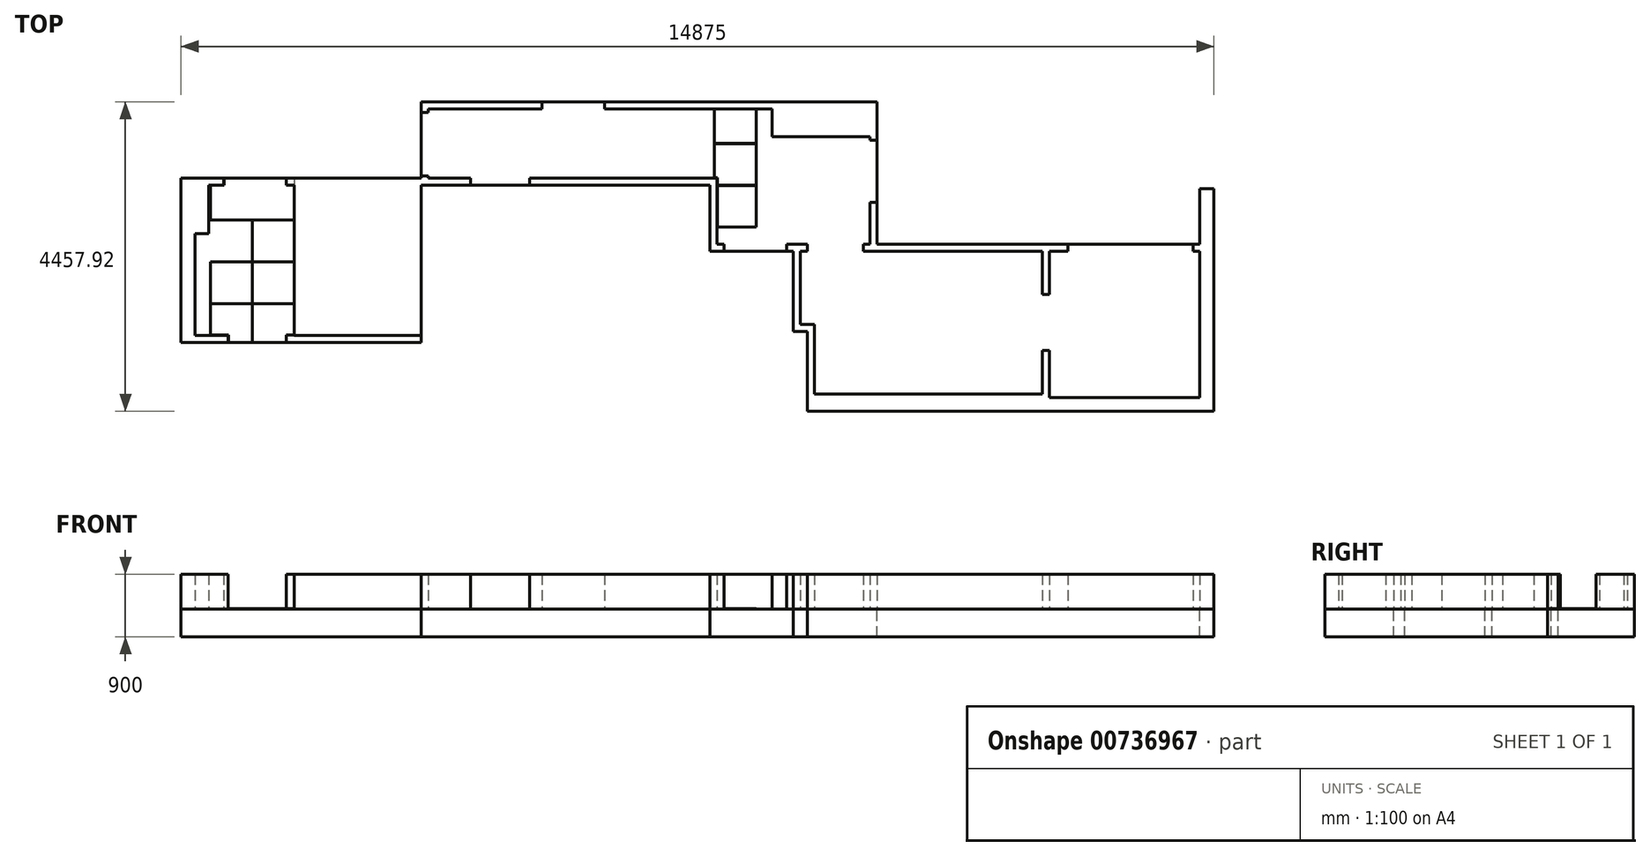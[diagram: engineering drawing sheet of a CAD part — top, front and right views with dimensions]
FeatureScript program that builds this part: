
annotation { "Feature Type Name" : "Feature", "Feature Type Description" : "" }
export const myFeature = defineFeature(function(context is Context, id is Id, definition is map)
    precondition{}
    {
        {
            var Q0;
            Q0=qCreatedBy(makeId("Top.planeOp"),FACE);
            var sketch = newSketch(context, id + "F0", { "sketchPlane" : qUnion([Q0])});
            skLineSegment(sketch, "E0.top", {"start": v(0, 2200) * mm, "end": v(-100, 2200) * mm});
            skLineSegment(sketch, "E0.left", {"start": v(0, 92.08) * mm, "end": v(0, 2200) * mm});
            skLineSegment(sketch, "E1", {"start": v(-1900, 2200) * mm, "end": v(-2168.75, 2200) * mm});
            skLineSegment(sketch, "E2", {"start": v(-4650, 2300) * mm, "end": v(0, 2300) * mm});
            skLineSegment(sketch, "E3.bottom", {"start": v(-1900, 2300) * mm, "end": v(-100, 2300) * mm});
            skLineSegment(sketch, "E3.left", {"start": v(-1900, 2300) * mm, "end": v(-1900, 2200) * mm});
            skLineSegment(sketch, "E3.right", {"start": v(-100, 2300) * mm, "end": v(-100, 2200) * mm});
            skLineSegment(sketch, "E4.bottom", {"start": v(-4650, 2200) * mm, "end": v(-4750, 2200) * mm});
            skLineSegment(sketch, "E4.top", {"start": v(-4650, 4350) * mm, "end": v(-4750, 4350) * mm});
            skLineSegment(sketch, "E4.left", {"start": v(-4650, 2300) * mm, "end": v(-4650, 4350) * mm});
            skLineSegment(sketch, "E4.right", {"start": v(-4750, 2300) * mm, "end": v(-4750, 2900) * mm});
            skLineSegment(sketch, "E5.bottom", {"start": v(-4750, 2900) * mm, "end": v(-4650, 2900) * mm});
            skLineSegment(sketch, "E5.top", {"start": v(-4750, 3800) * mm, "end": v(-4650, 3800) * mm});
            skLineSegment(sketch, "E5.right", {"start": v(-4650, 2900) * mm, "end": v(-4650, 3800) * mm});
            skLineSegment(sketch, "E6.bottom", {"start": v(-4650, 4350) * mm, "end": v(-8575, 4350) * mm});
            skLineSegment(sketch, "E6.top", {"start": v(-6160, 4250) * mm, "end": v(-8575, 4250) * mm});
            skLineSegment(sketch, "E6.left", {"start": v(-4650, 4350) * mm, "end": v(-4650, 4250) * mm});
            skLineSegment(sketch, "E6.right", {"start": v(-8575, 4350) * mm, "end": v(-8575, 4250) * mm});
            skLineSegment(sketch, "E7.trimOffspring", {"start": v(-4750, 3800) * mm, "end": v(-4750, 3850) * mm});
            skLineSegment(sketch, "E8.bottom", {"start": v(-8575, 4350) * mm, "end": v(-9475, 4350) * mm});
            skLineSegment(sketch, "E8.left", {"start": v(-8575, 4350) * mm, "end": v(-8575, 4245.37) * mm});
            skLineSegment(sketch, "E8.right", {"start": v(-9475, 4350) * mm, "end": v(-9475, 4250) * mm});
            skLineSegment(sketch, "E9.bottom", {"start": v(-9475, 4350) * mm, "end": v(-11115, 4350) * mm});
            skLineSegment(sketch, "E9.top", {"start": v(-9475, 4250) * mm, "end": v(-11115, 4250) * mm});
            skLineSegment(sketch, "E10.bottom", {"start": v(-11115, 4350) * mm, "end": v(-11215, 4350) * mm});
            skLineSegment(sketch, "E10.left", {"start": v(-11115, 4250) * mm, "end": v(-11115, 4195) * mm});
            skLineSegment(sketch, "E10.right", {"start": v(-11215, 4350) * mm, "end": v(-11215, 3250) * mm});
            skLineSegment(sketch, "E11.bottom", {"start": v(-11215, 4195) * mm, "end": v(-11115, 4195) * mm});
            skLineSegment(sketch, "E11.top", {"start": v(-11215, 3285) * mm, "end": v(-11115, 3285) * mm});
            skLineSegment(sketch, "E11.left", {"start": v(-11215, 4195) * mm, "end": v(-11215, 3285) * mm});
            skLineSegment(sketch, "E12.trimOffspring", {"start": v(-11115, 3285) * mm, "end": v(-11115, 3250) * mm});
            skLineSegment(sketch, "E13.bottom", {"start": v(-11115, 3250) * mm, "end": v(-10505.7, 3250) * mm});
            skLineSegment(sketch, "E13.top", {"start": v(-11215, 3150) * mm, "end": v(-7055.7, 3150) * mm});
            skLineSegment(sketch, "E13.right", {"start": v(-6955.7, 3250) * mm, "end": v(-6955.7, 3150) * mm});
            skLineSegment(sketch, "E14.bottom", {"start": v(-13045, 3150) * mm, "end": v(-13160, 3150) * mm});
            skLineSegment(sketch, "E14.top", {"start": v(-11215, 885) * mm, "end": v(-14475, 885) * mm});
            skLineSegment(sketch, "E14.left", {"start": v(-11215, 3150) * mm, "end": v(-11215, 885) * mm});
            skLineSegment(sketch, "E14.right", {"start": v(-14475, 2450) * mm, "end": v(-14475, 985) * mm});
            skLineSegment(sketch, "E15.top", {"start": v(-11215, 985) * mm, "end": v(-13155, 985) * mm});
            skLineSegment(sketch, "E15.left", {"start": v(-11215, 3285) * mm, "end": v(-11215, 985) * mm});
            skLineSegment(sketch, "E15.right", {"start": v(-14675, 3250) * mm, "end": v(-14675, 985) * mm});
            skLineSegment(sketch, "E16.top", {"start": v(-14475, 2450) * mm, "end": v(-14275, 2450) * mm});
            skLineSegment(sketch, "E16.right", {"start": v(-14275, 3150) * mm, "end": v(-14275, 2450) * mm});
            skLineSegment(sketch, "E17.top", {"start": v(-13045, 985) * mm, "end": v(-12945, 985) * mm});
            skLineSegment(sketch, "E17.left", {"start": v(-13045, 3150) * mm, "end": v(-13045, 985) * mm});
            skLineSegment(sketch, "E17.right", {"start": v(-12945, 3150) * mm, "end": v(-12945, 985) * mm});
            skLineSegment(sketch, "E18", {"start": v(-11215, 3250) * mm, "end": v(-14675, 3250) * mm});
            skLineSegment(sketch, "E19.top", {"start": v(-14675, 885) * mm, "end": v(-14475, 885) * mm});
            skLineSegment(sketch, "E19.left", {"start": v(-14675, 985) * mm, "end": v(-14675, 885) * mm});
            skLineSegment(sketch, "E20.top", {"start": v(-13995, 885) * mm, "end": v(-13155, 885) * mm});
            skLineSegment(sketch, "E20.left", {"start": v(-13995, 985) * mm, "end": v(-13995, 885) * mm});
            skLineSegment(sketch, "E20.right", {"start": v(-13155, 985) * mm, "end": v(-13155, 885) * mm});
            skLineSegment(sketch, "E21.bottom", {"start": v(-14060, 3250) * mm, "end": v(-13160, 3250) * mm});
            skLineSegment(sketch, "E21.left", {"start": v(-14060, 3250) * mm, "end": v(-14060, 3150) * mm});
            skLineSegment(sketch, "E21.right", {"start": v(-13160, 3250) * mm, "end": v(-13160, 3150) * mm});
            skLineSegment(sketch, "E22.trimOffspring", {"start": v(-14060, 3150) * mm, "end": v(-14275, 3150) * mm});
            skLineSegment(sketch, "E23.trimOffspring", {"start": v(-13995, 985) * mm, "end": v(-14475, 985) * mm});
            skLineSegment(sketch, "E24.top", {"start": v(-6955.7, 2300) * mm, "end": v(-6855.7, 2300) * mm});
            skLineSegment(sketch, "E24.left", {"start": v(-6955.7, 3250) * mm, "end": v(-6955.7, 2300) * mm});
            skLineSegment(sketch, "E24.right", {"start": v(-4650, 3250) * mm, "end": v(-4650, 2300) * mm});
            skLineSegment(sketch, "E25.bottom", {"start": v(-7055.7, 3250) * mm, "end": v(-6955.7, 3250) * mm});
            skLineSegment(sketch, "E25.top", {"start": v(-7055.7, 2200) * mm, "end": v(-5855.7, 2200) * mm});
            skLineSegment(sketch, "E25.left", {"start": v(-7055.7, 3150) * mm, "end": v(-7055.7, 2200) * mm});
            skLineSegment(sketch, "E26.top", {"start": v(-6855.7, 2200) * mm, "end": v(-5955.7, 2200) * mm});
            skLineSegment(sketch, "E26.left", {"start": v(-6855.7, 2300) * mm, "end": v(-6855.7, 2200) * mm});
            skLineSegment(sketch, "E26.right", {"start": v(-5955.7, 2300) * mm, "end": v(-5955.7, 2200) * mm});
            skLineSegment(sketch, "E27.trimOffspring", {"start": v(-5955.7, 2300) * mm, "end": v(-5655.7, 2300) * mm});
            skLineSegment(sketch, "E28.bottom", {"start": v(-12945, 3150) * mm, "end": v(-11215, 3150) * mm});
            skLineSegment(sketch, "E28.top", {"start": v(-12945, 3250) * mm, "end": v(-11215, 3250) * mm});
            skLineSegment(sketch, "E29.top", {"start": v(-6160, 3850) * mm, "end": v(-4750, 3850) * mm});
            skLineSegment(sketch, "E29.left", {"start": v(-6160, 4250) * mm, "end": v(-6160, 3850) * mm});
            skPoint(sketch, "E30.orphan", {"position": v(-4750, 4250) * mm});
            skLineSegment(sketch, "E31.left", {"start": v(-5655.7, 2300) * mm, "end": v(-5655.7, 2200) * mm});
            skLineSegment(sketch, "E31.right", {"start": v(-4850, 2300) * mm, "end": v(-4850, 2200) * mm});
            skLineSegment(sketch, "E32.left", {"start": v(-5855.7, 2200) * mm, "end": v(-5855.7, 1042.08) * mm});
            skLineSegment(sketch, "E32.right", {"start": v(-5755.7, 2200) * mm, "end": v(-5755.7, 1142.08) * mm});
            skLineSegment(sketch, "E33.bottom", {"start": v(0, 3100) * mm, "end": v(200, 3100) * mm});
            skLineSegment(sketch, "E33.left", {"start": v(0, 3100) * mm, "end": v(0, 2300) * mm});
            skLineSegment(sketch, "E33.right", {"start": v(200, 3100) * mm, "end": v(200, 0) * mm});
            skLineSegment(sketch, "E34.trimOffspring", {"start": v(0, 2200) * mm, "end": v(0, 92.08) * mm});
            skLineSegment(sketch, "E35.left", {"start": v(0, 0) * mm, "end": v(0, 0) * mm});
            skLineSegment(sketch, "E36.trimOffspring", {"start": v(-4850, 2300) * mm, "end": v(-4750, 2300) * mm});
            skLineSegment(sketch, "E37.trimOffspring", {"start": v(-4850, 2200) * mm, "end": v(-4650, 2200) * mm});
            skLineSegment(sketch, "E38.top", {"start": v(-5655.7, -107.92) * mm, "end": v(200, -107.92) * mm});
            skLineSegment(sketch, "E38.right", {"start": v(200, 142.08) * mm, "end": v(200, -107.92) * mm});
            skLineSegment(sketch, "E39.bottom", {"start": v(-5855.7, 1042.08) * mm, "end": v(-5655.7, 1042.08) * mm});
            skLineSegment(sketch, "E39.right", {"start": v(-5655.7, 1042.08) * mm, "end": v(-5655.7, -107.92) * mm});
            skLineSegment(sketch, "E40.bottom", {"start": v(-5755.7, 1142.08) * mm, "end": v(-5555.7, 1142.08) * mm});
            skLineSegment(sketch, "E40.right", {"start": v(-5555.7, 1142.08) * mm, "end": v(-5555.7, 142.08) * mm});
            skLineSegment(sketch, "E41.trimOffspring", {"start": v(-5555.7, 142.08) * mm, "end": v(-2268.75, 142.08) * mm});
            skLineSegment(sketch, "E42.left", {"start": v(-2168.75, 2200) * mm, "end": v(-2168.75, 1575) * mm});
            skLineSegment(sketch, "E42.right", {"start": v(-2268.75, 2200) * mm, "end": v(-2268.75, 1575) * mm});
            skLineSegment(sketch, "E43.trimOffspring", {"start": v(-2268.75, 2200) * mm, "end": v(-4650, 2200) * mm});
            skLineSegment(sketch, "E44.trimOffspring", {"start": v(0, 142.08) * mm, "end": v(200, 142.08) * mm});
            skLineSegment(sketch, "E45.trimOffspring", {"start": v(-2268.75, 142.08) * mm, "end": v(-5555.7, 142.08) * mm});
            skLineSegment(sketch, "E46", {"start": v(-4482.54, 1242.08) * mm, "end": v(-1007.3, 1242.08) * mm, "construction": true});
            skLineSegment(sketch, "E47.bottom", {"start": v(-2268.75, 1575) * mm, "end": v(-2168.75, 1575) * mm});
            skLineSegment(sketch, "E47.top", {"start": v(-2268.75, 767.08) * mm, "end": v(-2168.75, 767.08) * mm});
            skLineSegment(sketch, "E48.bottom", {"start": v(-2268.75, 1575) * mm, "end": v(-2268.75, 1575) * mm});
            skLineSegment(sketch, "E48.top", {"start": v(-2268.75, 767.08) * mm, "end": v(-2268.75, 767.08) * mm});
            skLineSegment(sketch, "E49.top", {"start": v(-2168.75, 92.08) * mm, "end": v(0, 92.08) * mm});
            skLineSegment(sketch, "E49.left", {"start": v(-2168.75, 142.08) * mm, "end": v(-2168.75, 92.08) * mm});
            skLineSegment(sketch, "E49.right", {"start": v(0, 142.08) * mm, "end": v(0, 92.08) * mm});
            skLineSegment(sketch, "E50.trimOffspring", {"start": v(-5755.7, 2200) * mm, "end": v(-5655.7, 2200) * mm});
            skLineSegment(sketch, "E51.trimOffspring", {"start": v(-2168.75, 767.08) * mm, "end": v(-2168.75, 142.08) * mm});
            skLineSegment(sketch, "E52.trimOffspring", {"start": v(-2268.75, 767.08) * mm, "end": v(-2268.75, 142.08) * mm});
            skLineSegment(sketch, "E53.top", {"start": v(-10505.7, 3150) * mm, "end": v(-9655.7, 3150) * mm});
            skLineSegment(sketch, "E53.left", {"start": v(-10505.7, 3250) * mm, "end": v(-10505.7, 3150) * mm});
            skLineSegment(sketch, "E53.right", {"start": v(-9655.7, 3250) * mm, "end": v(-9655.7, 3150) * mm});
            skLineSegment(sketch, "E54.trimOffspring", {"start": v(-9655.7, 3250) * mm, "end": v(-6955.7, 3250) * mm});
            skSolve(sketch);
        }
        {
            var Q0;
            Q0 = qSketchRegion(id + "F0", true);
            extrude(context, id + "F1", {"entities" : qUnion([Q0]), "oppositeDirection" : true, "depth" : 400 * mm, "offsetDistance" : 25 * mm});
        }
        {
            var Q0;
            Q0=makeQuery(id+"F0.imprint","IMPRINT",FACE,{"disambiguationData":[TD([[makeQuery(id+"F0.imprint","IMPRINT",EDGE,{"derivedFrom":sQuery(id+"F0.wireOp",EDGE,"E9.bottom")}),1.0]])]});
            var Q1;
            Q1=makeQuery(id+"F0.imprint","IMPRINT",FACE,{"disambiguationData":[TD([[makeQuery(id+"F0.imprint","IMPRINT",EDGE,{"derivedFrom":sQuery(id+"F0.wireOp",EDGE,"E4.left")}),1.0]])]});
            var Q2;
            {var subQ4=sQuery(id+"F0.wireOp",EDGE,"E11.top");Q2=makeQuery(id+"F0.imprint","IMPRINT",FACE,{"disambiguationData":[TD([[makeQuery(id+"F0.imprint","IMPRINT",EDGE,{"derivedFrom":subQ4}),-1.0]])]});}
            var Q3;
            Q3=makeQuery(id+"F0.imprint","IMPRINT",FACE,{"disambiguationData":[TD([[makeQuery(id+"F0.imprint","IMPRINT",EDGE,{"derivedFrom":sQuery(id+"F0.wireOp",EDGE,"E14.bottom")}),-1.0]])]});
            var Q4;
            Q4=makeQuery(id+"F0.imprint","IMPRINT",FACE,{"disambiguationData":[TD([[makeQuery(id+"F0.imprint","IMPRINT",EDGE,{"derivedFrom":sQuery(id+"F0.wireOp",EDGE,"E14.right")}),-1.0]])]});
            var Q5;
            {var subQ1=sQuery(id+"F0.wireOp",EDGE,"E14.left");Q5=makeQuery(id+"F0.imprint","IMPRINT",FACE,{"disambiguationData":[TD([[makeQuery(id+"F0.imprint","IMPRINT",EDGE,{"derivedFrom":subQ1}),-1.0]])]});}
            var Q6;
            {var subQ7=sQuery(id+"F0.wireOp",EDGE,"E26.right");Q6=makeQuery(id+"F0.imprint","IMPRINT",FACE,{"disambiguationData":[TD([[makeQuery(id+"F0.imprint","IMPRINT",EDGE,{"derivedFrom":subQ7}),1.0]])]});}
            var Q7;
            Q7=makeQuery(id+"F0.imprint","IMPRINT",FACE,{"disambiguationData":[TD([[makeQuery(id+"F0.imprint","IMPRINT",EDGE,{"derivedFrom":sQuery(id+"F0.wireOp",EDGE,"E1")}),-1.0]])]});
            var Q8;
            {var subQ0=sQuery(id+"F0.wireOp",EDGE,"E0.top");Q8=makeQuery(id+"F0.imprint","IMPRINT",FACE,{"disambiguationData":[TD([[makeQuery(id+"F0.imprint","IMPRINT",EDGE,{"derivedFrom":subQ0}),-1.0]])]});}
            var Q9;
            {var subQ1=sQuery(id+"F0.wireOp",EDGE,"E24.top");Q9=makeQuery(id+"F0.imprint","IMPRINT",FACE,{"disambiguationData":[TD([[makeQuery(id+"F0.imprint","IMPRINT",EDGE,{"derivedFrom":subQ1}),-1.0]])]});}
            extrude(context, id + "F2", {"entities" : qUnion([Q0, Q1, Q2, Q3, Q4, Q5, Q6, Q7, Q8, Q9]), "depth" : 500 * mm, "offsetDistance" : 25 * mm});
        }
        {
            var Q0;
            Q0=makeQuery(id+"F1.opExtrude","CAP_FACE",FACE,{"disambiguationData":[OSD([sQuery(id+"F0.wireOp",EDGE,"E2"),sQuery(id+"F0.wireOp",EDGE,"E3.bottom"),sQuery(id+"F0.wireOp",EDGE,"E4.left"),sQuery(id+"F0.wireOp",EDGE,"E5.right"),sQuery(id+"F0.wireOp",EDGE,"E6.bottom"),sQuery(id+"F0.wireOp",EDGE,"E6.left"),sQuery(id+"F0.wireOp",EDGE,"E8.bottom"),sQuery(id+"F0.wireOp",EDGE,"E9.bottom"),sQuery(id+"F0.wireOp",EDGE,"E10.bottom"),sQuery(id+"F0.wireOp",EDGE,"E10.right"),sQuery(id+"F0.wireOp",EDGE,"E11.left"),sQuery(id+"F0.wireOp",EDGE,"E13.top"),sQuery(id+"F0.wireOp",EDGE,"E14.top"),sQuery(id+"F0.wireOp",EDGE,"E14.left"),sQuery(id+"F0.wireOp",EDGE,"E15.left"),sQuery(id+"F0.wireOp",EDGE,"E15.right"),sQuery(id+"F0.wireOp",EDGE,"E18"),sQuery(id+"F0.wireOp",EDGE,"E19.top"),sQuery(id+"F0.wireOp",EDGE,"E19.left"),sQuery(id+"F0.wireOp",EDGE,"E20.top"),sQuery(id+"F0.wireOp",EDGE,"E21.bottom"),sQuery(id+"F0.wireOp",EDGE,"E25.top"),sQuery(id+"F0.wireOp",EDGE,"E25.left"),sQuery(id+"F0.wireOp",EDGE,"E24.right"),sQuery(id+"F0.wireOp",EDGE,"E26.top"),sQuery(id+"F0.wireOp",EDGE,"E28.top"),sQuery(id+"F0.wireOp",EDGE,"E33.bottom"),sQuery(id+"F0.wireOp",EDGE,"E33.left"),sQuery(id+"F0.wireOp",EDGE,"E33.right"),sQuery(id+"F0.wireOp",EDGE,"E32.left"),sQuery(id+"F0.wireOp",EDGE,"E38.top"),sQuery(id+"F0.wireOp",EDGE,"E38.right"),sQuery(id+"F0.wireOp",EDGE,"E39.bottom"),sQuery(id+"F0.wireOp",EDGE,"E39.right")])],"isStart":true});
            var sketch = newSketch(context, id + "F3", { "sketchPlane" : qUnion([Q0])});
            skLineSegment(sketch, "E55", {"start": v(-11232.86, 3750) * mm, "end": v(-6657.9, 3750) * mm, "construction": true});
            skLineSegment(sketch, "E56", {"start": v(-6601.23, 1100) * mm, "end": v(377.65, 1100) * mm, "construction": true});
            skLineSegment(sketch, "E57", {"start": v(-13646.5, 3585.93) * mm, "end": v(-13646.5, 518.44) * mm, "construction": true});
            skLineSegment(sketch, "E58.bottom", {"start": v(-13646.5, 2647) * mm, "end": v(-13046.5, 2647) * mm});
            skLineSegment(sketch, "E58.top", {"start": v(-13646.5, 2047) * mm, "end": v(-13046.5, 2047) * mm});
            skLineSegment(sketch, "E58.left", {"start": v(-13646.5, 2647) * mm, "end": v(-13646.5, 2047) * mm});
            skLineSegment(sketch, "E58.right", {"start": v(-13046.5, 2647) * mm, "end": v(-13046.5, 2047) * mm});
            skLineSegment(sketch, "E59.bottom", {"start": v(-13649.5, 2647) * mm, "end": v(-14249.5, 2647) * mm});
            skLineSegment(sketch, "E59.top", {"start": v(-13649.5, 2047) * mm, "end": v(-14249.5, 2047) * mm});
            skLineSegment(sketch, "E59.right", {"start": v(-14249.5, 2647) * mm, "end": v(-14249.5, 2047) * mm});
            skLineSegment(sketch, "E60.bottom", {"start": v(-14249.5, 2647) * mm, "end": v(-13649.5, 2647) * mm});
            skLineSegment(sketch, "E60.top", {"start": v(-14249.5, 2047) * mm, "end": v(-13649.5, 2047) * mm});
            skLineSegment(sketch, "E60.right", {"start": v(-13649.5, 2647) * mm, "end": v(-13649.5, 2047) * mm});
            skLineSegment(sketch, "E61.bottom", {"start": v(-13646.5, 3250) * mm, "end": v(-13042.88, 3250) * mm});
            skLineSegment(sketch, "E61.top", {"start": v(-13646.5, 2650) * mm, "end": v(-13042.88, 2650) * mm});
            skLineSegment(sketch, "E61.left", {"start": v(-13646.5, 3250) * mm, "end": v(-13646.5, 2650) * mm});
            skLineSegment(sketch, "E61.right", {"start": v(-13042.88, 3250) * mm, "end": v(-13042.88, 2650) * mm});
            skLineSegment(sketch, "E62.bottom", {"start": v(-14249.5, 2650) * mm, "end": v(-13646.5, 2650) * mm});
            skLineSegment(sketch, "E62.top", {"start": v(-14057, 3250) * mm, "end": v(-13646.5, 3250) * mm});
            skLineSegment(sketch, "E62.left", {"start": v(-14249.5, 2650) * mm, "end": v(-14249.5, 3147) * mm});
            skLineSegment(sketch, "E62.right", {"start": v(-13646.5, 2650) * mm, "end": v(-13646.5, 3250) * mm});
            skLineSegment(sketch, "E63", {"start": v(-14249.5, 3147) * mm, "end": v(-14057, 3147) * mm});
            skLineSegment(sketch, "E64", {"start": v(-14057, 3147) * mm, "end": v(-14057, 3250) * mm});
            skLineSegment(sketch, "E65", {"start": v(-13163, 3250) * mm, "end": v(-13163, 3147) * mm});
            skLineSegment(sketch, "E66", {"start": v(-13163, 3147) * mm, "end": v(-13042.88, 3147) * mm});
            skLineSegment(sketch, "E67.bottom", {"start": v(-14249.5, 2044) * mm, "end": v(-13649.5, 2044) * mm});
            skLineSegment(sketch, "E67.top", {"start": v(-14249.5, 1444) * mm, "end": v(-13649.5, 1444) * mm});
            skLineSegment(sketch, "E67.left", {"start": v(-14249.5, 2044) * mm, "end": v(-14249.5, 1444) * mm});
            skLineSegment(sketch, "E67.right", {"start": v(-13649.5, 2044) * mm, "end": v(-13649.5, 1444) * mm});
            skLineSegment(sketch, "E68.bottom", {"start": v(-13646.5, 2044) * mm, "end": v(-13046.5, 2044) * mm});
            skLineSegment(sketch, "E68.top", {"start": v(-13646.5, 1444) * mm, "end": v(-13046.5, 1444) * mm});
            skLineSegment(sketch, "E68.left", {"start": v(-13646.5, 2044) * mm, "end": v(-13646.5, 1444) * mm});
            skLineSegment(sketch, "E68.right", {"start": v(-13046.5, 2044) * mm, "end": v(-13046.5, 1444) * mm});
            skLineSegment(sketch, "E69.bottom", {"start": v(-14249.5, 1441) * mm, "end": v(-13649.5, 1441) * mm});
            skLineSegment(sketch, "E69.left", {"start": v(-14249.5, 1441) * mm, "end": v(-14249.5, 988) * mm});
            skLineSegment(sketch, "E69.right", {"start": v(-13649.5, 1441) * mm, "end": v(-13649.5, 885) * mm});
            skLineSegment(sketch, "E70.bottom", {"start": v(-13646.5, 1441) * mm, "end": v(-13046.5, 1441) * mm});
            skLineSegment(sketch, "E70.left", {"start": v(-13646.5, 1441) * mm, "end": v(-13646.5, 841) * mm});
            skLineSegment(sketch, "E70.right", {"start": v(-13046.5, 1441) * mm, "end": v(-13046.5, 988) * mm});
            skLineSegment(sketch, "E71", {"start": v(-14249.5, 988) * mm, "end": v(-13992, 988) * mm});
            skLineSegment(sketch, "E72", {"start": v(-13992, 988) * mm, "end": v(-13992, 885) * mm});
            skLineSegment(sketch, "E73", {"start": v(-13158, 885) * mm, "end": v(-13158, 988) * mm});
            skLineSegment(sketch, "E74", {"start": v(-13158, 988) * mm, "end": v(-13046.5, 988) * mm});
            skLineSegment(sketch, "E75", {"start": v(-13992, 885) * mm, "end": v(-13649.5, 885) * mm});
            skLineSegment(sketch, "E76", {"start": v(-13646.5, 885) * mm, "end": v(-13158, 885) * mm});
            skLineSegment(sketch, "E77.bottom", {"start": v(-6950.7, 3148.5) * mm, "end": v(-6394, 3148.5) * mm});
            skLineSegment(sketch, "E77.top", {"start": v(-6954.2, 3748.5) * mm, "end": v(-6394, 3748.5) * mm});
            skLineSegment(sketch, "E78.bottom", {"start": v(-6950.7, 3145.5) * mm, "end": v(-6394, 3145.5) * mm});
            skLineSegment(sketch, "E78.top", {"start": v(-6950.7, 2545.5) * mm, "end": v(-6394, 2545.5) * mm});
            skLineSegment(sketch, "E78.left", {"start": v(-6950.7, 3145.5) * mm, "end": v(-6950.7, 2545.5) * mm});
            skLineSegment(sketch, "E79.bottom", {"start": v(-6954.2, 3751.5) * mm, "end": v(-6394, 3751.5) * mm});
            skLineSegment(sketch, "E79.top", {"start": v(-6954.2, 4247) * mm, "end": v(-6394, 4247) * mm});
            skLineSegment(sketch, "E80.left", {"start": v(-11215, 3751.5) * mm, "end": v(-11215, 4190) * mm});
            skLineSegment(sketch, "E80.right", {"start": v(-10615, 3751.5) * mm, "end": v(-10615, 4244.92) * mm});
            skLineSegment(sketch, "E81.bottom", {"start": v(-11215, 4190) * mm, "end": v(-11110, 4190) * mm});
            skLineSegment(sketch, "E81.right", {"start": v(-11110, 4190) * mm, "end": v(-11110, 4244.92) * mm});
            skLineSegment(sketch, "E82", {"start": v(-11215, 3751.5) * mm, "end": v(-10615, 3751.5) * mm});
            skPoint(sketch, "E83.orphan", {"position": v(-11215, 3800) * mm});
            skLineSegment(sketch, "E84.MirrorCS", {"start": v(-11215, 3748.5) * mm, "end": v(-10615, 3748.5) * mm});
            skLineSegment(sketch, "E85.MirrorCS", {"start": v(-10615, 3748.5) * mm, "end": v(-10615, 3255) * mm});
            skLineSegment(sketch, "E86.MirrorCS", {"start": v(-11110, 3290.7) * mm, "end": v(-11110, 3255) * mm});
            skLineSegment(sketch, "E87.MirrorCS", {"start": v(-11215, 3748.5) * mm, "end": v(-11215, 3310) * mm});
            skLineSegment(sketch, "E88", {"start": v(-11215, 3290.7) * mm, "end": v(-11110, 3290.7) * mm});
            skPoint(sketch, "E89.orphan", {"position": v(-11110, 3310) * mm});
            skLineSegment(sketch, "E90", {"start": v(-11215, 3290.7) * mm, "end": v(-11215, 3310) * mm});
            skLineSegment(sketch, "E91", {"start": v(-11110, 3255) * mm, "end": v(-10615, 3255) * mm});
            skPoint(sketch, "E92.MirrorCS.start.orphan", {"position": v(-11110, 3248) * mm});
            skPoint(sketch, "E93.orphan", {"position": v(-10615, 3248) * mm});
            skLineSegment(sketch, "E94", {"start": v(-11110, 4244.92) * mm, "end": v(-10615, 4244.92) * mm});
            skPoint(sketch, "E95.orphan", {"position": v(-10615, 4252) * mm});
            skPoint(sketch, "E96.orphan", {"position": v(-11110, 4252) * mm});
            skLineSegment(sketch, "E97.bottom", {"start": v(-10612, 4244.92) * mm, "end": v(-10012, 4244.92) * mm});
            skLineSegment(sketch, "E97.top", {"start": v(-10612, 3751.5) * mm, "end": v(-10012, 3751.5) * mm});
            skLineSegment(sketch, "E97.left", {"start": v(-10612, 4244.92) * mm, "end": v(-10612, 3751.5) * mm});
            skLineSegment(sketch, "E97.right", {"start": v(-10012, 4244.92) * mm, "end": v(-10012, 3751.5) * mm});
            skLineSegment(sketch, "E98.bottom", {"start": v(-10612, 3748.5) * mm, "end": v(-10012, 3748.5) * mm});
            skLineSegment(sketch, "E98.top", {"start": v(-10503.7, 3148.5) * mm, "end": v(-10012, 3148.5) * mm});
            skLineSegment(sketch, "E98.left", {"start": v(-10612, 3748.5) * mm, "end": v(-10612, 3255) * mm});
            skLineSegment(sketch, "E98.right", {"start": v(-10012, 3748.5) * mm, "end": v(-10012, 3148.5) * mm});
            skLineSegment(sketch, "E99.bottom", {"start": v(-10612, 3255) * mm, "end": v(-10503.7, 3255) * mm});
            skLineSegment(sketch, "E99.top", {"start": v(-10615, 3148.5) * mm, "end": v(-10612, 3148.5) * mm});
            skLineSegment(sketch, "E99.right", {"start": v(-10503.7, 3255) * mm, "end": v(-10503.7, 3148.5) * mm});
            skLineSegment(sketch, "E100.bottom", {"start": v(-10009, 3751.5) * mm, "end": v(-9409, 3751.5) * mm});
            skLineSegment(sketch, "E100.top", {"start": v(-10009, 4244.92) * mm, "end": v(-9468.1, 4244.92) * mm});
            skLineSegment(sketch, "E100.left", {"start": v(-10009, 3751.5) * mm, "end": v(-10009, 4244.92) * mm});
            skLineSegment(sketch, "E100.right", {"start": v(-9409, 3751.5) * mm, "end": v(-9409, 4244.92) * mm});
            skLineSegment(sketch, "E101.top", {"start": v(-9468.1, 4350) * mm, "end": v(-9409, 4350) * mm});
            skLineSegment(sketch, "E101.left", {"start": v(-9468.1, 4244.92) * mm, "end": v(-9468.1, 4350) * mm});
            skLineSegment(sketch, "E101.right", {"start": v(-9409, 4244.92) * mm, "end": v(-9409, 4350) * mm});
            skPoint(sketch, "E102.0", {"position": v(-9475, 4300) * mm});
            skLineSegment(sketch, "E103.0", {"start": v(-9475, 4350) * mm, "end": v(-9475, 4250) * mm});
            skLineSegment(sketch, "E104.bottom", {"start": v(-10009, 3748.5) * mm, "end": v(-9409, 3748.5) * mm});
            skLineSegment(sketch, "E104.top", {"start": v(-10009, 3150) * mm, "end": v(-9660.7, 3150) * mm});
            skLineSegment(sketch, "E104.left", {"start": v(-10009, 3748.5) * mm, "end": v(-10009, 3150) * mm});
            skLineSegment(sketch, "E104.right", {"start": v(-9409, 3748.5) * mm, "end": v(-9409, 3255) * mm});
            skLineSegment(sketch, "E105.top", {"start": v(-9660.7, 3255) * mm, "end": v(-9409, 3255) * mm});
            skLineSegment(sketch, "E105.left", {"start": v(-9660.7, 3150) * mm, "end": v(-9660.7, 3255) * mm});
            skLineSegment(sketch, "E106.bottom", {"start": v(-9406, 3751.5) * mm, "end": v(-8806, 3751.5) * mm});
            skLineSegment(sketch, "E106.top", {"start": v(-9406, 4350) * mm, "end": v(-8806, 4350) * mm});
            skLineSegment(sketch, "E106.left", {"start": v(-9406, 3751.5) * mm, "end": v(-9406, 4350) * mm});
            skLineSegment(sketch, "E106.right", {"start": v(-8806, 3751.5) * mm, "end": v(-8806, 4350) * mm});
            skLineSegment(sketch, "E107.bottom", {"start": v(-9406, 3748.5) * mm, "end": v(-8806, 3748.5) * mm});
            skLineSegment(sketch, "E107.top", {"start": v(-9406, 3255) * mm, "end": v(-8806, 3255) * mm});
            skLineSegment(sketch, "E107.left", {"start": v(-9406, 3748.5) * mm, "end": v(-9406, 3255) * mm});
            skLineSegment(sketch, "E107.right", {"start": v(-8806, 3748.5) * mm, "end": v(-8806, 3255) * mm});
            skLineSegment(sketch, "E108.bottom", {"start": v(-8803, 3751.5) * mm, "end": v(-8203, 3751.5) * mm});
            skLineSegment(sketch, "E108.top", {"start": v(-8803, 4350) * mm, "end": v(-8580, 4350) * mm});
            skLineSegment(sketch, "E108.left", {"start": v(-8803, 3751.5) * mm, "end": v(-8803, 4350) * mm});
            skLineSegment(sketch, "E108.right", {"start": v(-8203, 3751.5) * mm, "end": v(-8203, 4245) * mm});
            skLineSegment(sketch, "E109.top", {"start": v(-8580, 4245) * mm, "end": v(-8203, 4245) * mm});
            skLineSegment(sketch, "E109.left", {"start": v(-8580, 4350) * mm, "end": v(-8580, 4245) * mm});
            skLineSegment(sketch, "E110.bottom", {"start": v(-8803, 3748.5) * mm, "end": v(-8203, 3748.5) * mm});
            skLineSegment(sketch, "E110.top", {"start": v(-8803, 3255) * mm, "end": v(-8203, 3255) * mm});
            skLineSegment(sketch, "E110.left", {"start": v(-8803, 3748.5) * mm, "end": v(-8803, 3255) * mm});
            skLineSegment(sketch, "E110.right", {"start": v(-8203, 3748.5) * mm, "end": v(-8203, 3255) * mm});
            skLineSegment(sketch, "E111.bottom", {"start": v(-8200, 3751.5) * mm, "end": v(-7600, 3751.5) * mm});
            skLineSegment(sketch, "E111.top", {"start": v(-8200, 4245) * mm, "end": v(-7600, 4245) * mm});
            skLineSegment(sketch, "E111.left", {"start": v(-8200, 3751.5) * mm, "end": v(-8200, 4245) * mm});
            skLineSegment(sketch, "E111.right", {"start": v(-7600, 3751.5) * mm, "end": v(-7600, 4245) * mm});
            skLineSegment(sketch, "E112.bottom", {"start": v(-8200, 3748.5) * mm, "end": v(-7600, 3748.5) * mm});
            skLineSegment(sketch, "E112.top", {"start": v(-8200, 3255) * mm, "end": v(-7600, 3255) * mm});
            skLineSegment(sketch, "E112.left", {"start": v(-8200, 3748.5) * mm, "end": v(-8200, 3255) * mm});
            skLineSegment(sketch, "E112.right", {"start": v(-7600, 3748.5) * mm, "end": v(-7600, 3255) * mm});
            skLineSegment(sketch, "E113.bottom", {"start": v(-7597, 3751.5) * mm, "end": v(-6997, 3751.5) * mm});
            skLineSegment(sketch, "E113.top", {"start": v(-7597, 4245) * mm, "end": v(-6997, 4245) * mm});
            skLineSegment(sketch, "E113.left", {"start": v(-7597, 3751.5) * mm, "end": v(-7597, 4245) * mm});
            skLineSegment(sketch, "E113.right", {"start": v(-6997, 3751.5) * mm, "end": v(-6997, 4245) * mm});
            skLineSegment(sketch, "E114.bottom", {"start": v(-7597, 3748.5) * mm, "end": v(-6997, 3748.5) * mm});
            skLineSegment(sketch, "E114.top", {"start": v(-7597, 3255) * mm, "end": v(-6997, 3255) * mm});
            skLineSegment(sketch, "E114.left", {"start": v(-7597, 3748.5) * mm, "end": v(-7597, 3255) * mm});
            skLineSegment(sketch, "E114.right", {"start": v(-6997, 3748.5) * mm, "end": v(-6997, 3255) * mm});
            skLineSegment(sketch, "E115.bottom", {"start": v(-6994, 4247) * mm, "end": v(-6394, 4247) * mm});
            skLineSegment(sketch, "E115.top", {"start": v(-6994, 3751.5) * mm, "end": v(-6394, 3751.5) * mm});
            skLineSegment(sketch, "E115.left", {"start": v(-6994, 4247) * mm, "end": v(-6994, 3751.5) * mm});
            skLineSegment(sketch, "E115.right", {"start": v(-6394, 4247) * mm, "end": v(-6394, 3751.5) * mm});
            skPoint(sketch, "E116.orphan", {"position": v(-6354.2, 4247) * mm});
            skLineSegment(sketch, "E117.bottom", {"start": v(-6994, 3748.5) * mm, "end": v(-6394, 3748.5) * mm});
            skLineSegment(sketch, "E117.left", {"start": v(-6994, 3748.5) * mm, "end": v(-6994, 3255) * mm});
            skLineSegment(sketch, "E117.right", {"start": v(-6394, 3748.5) * mm, "end": v(-6394, 3148.5) * mm});
            skLineSegment(sketch, "E118.bottom", {"start": v(-6997, 3255) * mm, "end": v(-6950.7, 3255) * mm});
            skLineSegment(sketch, "E118.right", {"start": v(-6950.7, 3255) * mm, "end": v(-6950.7, 3148.5) * mm});
            skLineSegment(sketch, "E119", {"start": v(-6394, 3145.5) * mm, "end": v(-6394, 2545.5) * mm});
            skPoint(sketch, "E120.orphan", {"position": v(-6354.2, 3148.5) * mm});
            skPoint(sketch, "E121.orphan", {"position": v(-6354.2, 2545.5) * mm});
            skPoint(sketch, "E122.orphan", {"position": v(-6354.2, 3748.5) * mm});
            skLineSegment(sketch, "E123.bottom", {"start": v(-6391, 3752.04) * mm, "end": v(-5791, 3752.04) * mm});
            skLineSegment(sketch, "E123.top", {"start": v(-6391, 4247) * mm, "end": v(-6165, 4247) * mm});
            skLineSegment(sketch, "E123.left", {"start": v(-6391, 3752.04) * mm, "end": v(-6391, 4247) * mm});
            skLineSegment(sketch, "E123.right", {"start": v(-5791, 3752.04) * mm, "end": v(-5791, 3845) * mm});
            skLineSegment(sketch, "E124.top", {"start": v(-6165, 3845) * mm, "end": v(-5791, 3845) * mm});
            skLineSegment(sketch, "E124.left", {"start": v(-6165, 4247) * mm, "end": v(-6165, 3845) * mm});
            skPoint(sketch, "E125.orphan", {"position": v(-5791, 4247) * mm});
            skLineSegment(sketch, "E126.bottom", {"start": v(-6391, 3748.5) * mm, "end": v(-5791, 3748.5) * mm});
            skLineSegment(sketch, "E126.top", {"start": v(-6391, 3148.5) * mm, "end": v(-5791, 3148.5) * mm});
            skLineSegment(sketch, "E126.left", {"start": v(-6391, 3748.5) * mm, "end": v(-6391, 3148.5) * mm});
            skLineSegment(sketch, "E126.right", {"start": v(-5791, 3748.5) * mm, "end": v(-5791, 3148.5) * mm});
            skLineSegment(sketch, "E127.bottom", {"start": v(-5788, 3752.04) * mm, "end": v(-5188, 3752.04) * mm});
            skLineSegment(sketch, "E127.top", {"start": v(-5788, 3148.5) * mm, "end": v(-5188, 3148.5) * mm});
            skLineSegment(sketch, "E127.left", {"start": v(-5788, 3748.5) * mm, "end": v(-5788, 3148.5) * mm});
            skLineSegment(sketch, "E127.right", {"start": v(-5188, 3748.5) * mm, "end": v(-5188, 3148.5) * mm});
            skLineSegment(sketch, "E128", {"start": v(-5788, 3748.5) * mm, "end": v(-5188, 3748.5) * mm});
            skLineSegment(sketch, "E129.bottom", {"start": v(-5188, 3752.04) * mm, "end": v(-5788, 3752.04) * mm});
            skLineSegment(sketch, "E129.top", {"start": v(-5188, 3845) * mm, "end": v(-5788, 3845) * mm});
            skLineSegment(sketch, "E129.left", {"start": v(-5188, 3752.04) * mm, "end": v(-5188, 3845) * mm});
            skLineSegment(sketch, "E129.right", {"start": v(-5788, 3752.04) * mm, "end": v(-5788, 3845) * mm});
            skLineSegment(sketch, "E130.bottom", {"start": v(-6391, 3145.5) * mm, "end": v(-5791, 3145.5) * mm});
            skLineSegment(sketch, "E130.top", {"start": v(-6391, 2545.5) * mm, "end": v(-5791, 2545.5) * mm});
            skLineSegment(sketch, "E130.left", {"start": v(-6391, 3145.5) * mm, "end": v(-6391, 2545.5) * mm});
            skLineSegment(sketch, "E131", {"start": v(-5791, 3145.5) * mm, "end": v(-5791, 2545.5) * mm});
            skPoint(sketch, "E132.orphan", {"position": v(-5788, 2545.5) * mm});
            skLineSegment(sketch, "E133.bottom", {"start": v(-5788, 3145.5) * mm, "end": v(-5188, 3145.5) * mm});
            skLineSegment(sketch, "E133.top", {"start": v(-5788, 2545.5) * mm, "end": v(-5188, 2545.5) * mm});
            skLineSegment(sketch, "E133.left", {"start": v(-5788, 3145.5) * mm, "end": v(-5788, 2545.5) * mm});
            skLineSegment(sketch, "E133.right", {"start": v(-5188, 3145.5) * mm, "end": v(-5188, 2545.5) * mm});
            skLineSegment(sketch, "E134.bottom", {"start": v(-5185, 3748.5) * mm, "end": v(-4650, 3748.5) * mm});
            skLineSegment(sketch, "E134.top", {"start": v(-5185, 3148.5) * mm, "end": v(-4650, 3148.5) * mm});
            skLineSegment(sketch, "E134.left", {"start": v(-5185, 3748.5) * mm, "end": v(-5185, 3148.5) * mm});
            skLineSegment(sketch, "E134.right", {"start": v(-4650, 3748.5) * mm, "end": v(-4650, 3148.5) * mm});
            skLineSegment(sketch, "E135.bottom", {"start": v(-5185, 3752.04) * mm, "end": v(-4650, 3752.04) * mm});
            skLineSegment(sketch, "E135.top", {"start": v(-5185, 3845) * mm, "end": v(-4755, 3845) * mm});
            skLineSegment(sketch, "E135.left", {"start": v(-5185, 3752.04) * mm, "end": v(-5185, 3845) * mm});
            skLineSegment(sketch, "E135.right", {"start": v(-4650, 3752.04) * mm, "end": v(-4650, 3798.52) * mm});
            skLineSegment(sketch, "E136.top", {"start": v(-4755, 3798.52) * mm, "end": v(-4650, 3798.52) * mm});
            skLineSegment(sketch, "E136.left", {"start": v(-4755, 3845) * mm, "end": v(-4755, 3798.52) * mm});
            skPoint(sketch, "E137.orphan", {"position": v(-4650, 3845) * mm});
            skLineSegment(sketch, "E138.bottom", {"start": v(-5185, 2545.5) * mm, "end": v(-4650, 2545.5) * mm});
            skLineSegment(sketch, "E138.top", {"start": v(-5185, 3145.5) * mm, "end": v(-4650, 3145.5) * mm});
            skLineSegment(sketch, "E138.left", {"start": v(-5185, 2545.5) * mm, "end": v(-5185, 3145.5) * mm});
            skLineSegment(sketch, "E138.right", {"start": v(-4650, 2545.5) * mm, "end": v(-4650, 3145.5) * mm});
            skLineSegment(sketch, "E139.bottom", {"start": v(-4755, 2545.5) * mm, "end": v(-4650, 2545.5) * mm});
            skLineSegment(sketch, "E139.top", {"start": v(-4755, 2905) * mm, "end": v(-4650, 2905) * mm});
            skLineSegment(sketch, "E139.left", {"start": v(-4755, 2545.5) * mm, "end": v(-4755, 2905) * mm});
            skLineSegment(sketch, "E139.right", {"start": v(-4650, 2545.5) * mm, "end": v(-4650, 2905) * mm});
            skLineSegment(sketch, "E140.0", {"start": v(-4750, 2900) * mm, "end": v(-4650, 2900) * mm});
            skLineSegment(sketch, "E141.0", {"start": v(-4750, 2300) * mm, "end": v(-4750, 2900) * mm});
            skLineSegment(sketch, "E142.bottom", {"start": v(-6950.7, 2542.5) * mm, "end": v(-6394, 2542.5) * mm});
            skLineSegment(sketch, "E142.top", {"start": v(-6850.7, 2200) * mm, "end": v(-6394, 2200) * mm});
            skLineSegment(sketch, "E142.left", {"start": v(-6950.7, 2542.5) * mm, "end": v(-6950.7, 2305) * mm});
            skLineSegment(sketch, "E142.right", {"start": v(-6391, 2542.5) * mm, "end": v(-6391, 2200) * mm});
            skLineSegment(sketch, "E143.bottom", {"start": v(-6950.7, 2305) * mm, "end": v(-6850.7, 2305) * mm});
            skLineSegment(sketch, "E143.right", {"start": v(-6850.7, 2305) * mm, "end": v(-6850.7, 2200) * mm});
            skLineSegment(sketch, "E144", {"start": v(-6394, 2542.5) * mm, "end": v(-6394, 2200) * mm});
            skLineSegment(sketch, "E145.bottom", {"start": v(-6391, 2542.5) * mm, "end": v(-5791, 2542.5) * mm});
            skLineSegment(sketch, "E145.top", {"start": v(-6391, 2200) * mm, "end": v(-5960.7, 2200) * mm});
            skLineSegment(sketch, "E145.right", {"start": v(-5791, 2542.5) * mm, "end": v(-5791, 2305) * mm});
            skLineSegment(sketch, "E146.top", {"start": v(-5960.7, 2305) * mm, "end": v(-5791, 2305) * mm});
            skLineSegment(sketch, "E146.left", {"start": v(-5960.7, 2200) * mm, "end": v(-5960.7, 2305) * mm});
            skPoint(sketch, "E147.orphan", {"position": v(-5791, 2200) * mm});
            skLineSegment(sketch, "E148.bottom", {"start": v(-5788, 2542.5) * mm, "end": v(-5188, 2542.5) * mm});
            skLineSegment(sketch, "E148.top", {"start": v(-5750.96, 1942.5) * mm, "end": v(-5188, 1942.5) * mm});
            skLineSegment(sketch, "E148.left", {"start": v(-5788, 2542.5) * mm, "end": v(-5788, 2305) * mm});
            skLineSegment(sketch, "E148.right", {"start": v(-5188, 2542.5) * mm, "end": v(-5188, 1942.5) * mm});
            skLineSegment(sketch, "E149.bottom", {"start": v(-5788, 2305) * mm, "end": v(-5648.53, 2305) * mm});
            skLineSegment(sketch, "E149.top", {"start": v(-5750.96, 2194.94) * mm, "end": v(-5648.53, 2194.94) * mm});
            skLineSegment(sketch, "E149.right", {"start": v(-5648.53, 2305) * mm, "end": v(-5648.53, 2194.94) * mm});
            skLineSegment(sketch, "E150", {"start": v(-5750.96, 2194.94) * mm, "end": v(-5750.96, 1942.5) * mm});
            skLineSegment(sketch, "E151.bottom", {"start": v(-5185, 2542.5) * mm, "end": v(-4585, 2542.5) * mm});
            skLineSegment(sketch, "E151.top", {"start": v(-5185, 1942.5) * mm, "end": v(-4585, 1942.5) * mm});
            skLineSegment(sketch, "E151.left", {"start": v(-5185, 2542.5) * mm, "end": v(-5185, 1942.5) * mm});
            skLineSegment(sketch, "E151.right", {"start": v(-4585, 2188.68) * mm, "end": v(-4585, 1942.5) * mm});
            skLineSegment(sketch, "E152.bottom", {"start": v(-4855.82, 2307.29) * mm, "end": v(-4750, 2307.29) * mm});
            skLineSegment(sketch, "E152.top", {"start": v(-4855.82, 2188.68) * mm, "end": v(-4585, 2188.68) * mm});
            skLineSegment(sketch, "E152.left", {"start": v(-4855.82, 2307.29) * mm, "end": v(-4855.82, 2188.68) * mm});
            skLineSegment(sketch, "E153.bottom", {"start": v(-5185, 1939.5) * mm, "end": v(-4585, 1939.5) * mm});
            skLineSegment(sketch, "E153.top", {"start": v(-5185, 1339.5) * mm, "end": v(-4585, 1339.5) * mm});
            skLineSegment(sketch, "E153.left", {"start": v(-5185, 1939.5) * mm, "end": v(-5185, 1339.5) * mm});
            skLineSegment(sketch, "E153.right", {"start": v(-4585, 1939.5) * mm, "end": v(-4585, 1339.5) * mm});
            skLineSegment(sketch, "E154.bottom", {"start": v(-5185, 1336.5) * mm, "end": v(-4585, 1336.5) * mm});
            skLineSegment(sketch, "E154.top", {"start": v(-5185, 736.5) * mm, "end": v(-4585, 736.5) * mm});
            skLineSegment(sketch, "E154.left", {"start": v(-5185, 1336.5) * mm, "end": v(-5185, 736.5) * mm});
            skLineSegment(sketch, "E154.right", {"start": v(-4585, 1336.5) * mm, "end": v(-4585, 736.5) * mm});
            skLineSegment(sketch, "E155.bottom", {"start": v(-4582, 1939.5) * mm, "end": v(-3982, 1939.5) * mm});
            skLineSegment(sketch, "E155.top", {"start": v(-4582, 1339.5) * mm, "end": v(-3982, 1339.5) * mm});
            skLineSegment(sketch, "E155.left", {"start": v(-4582, 1939.5) * mm, "end": v(-4582, 1339.5) * mm});
            skLineSegment(sketch, "E155.right", {"start": v(-3982, 1939.5) * mm, "end": v(-3982, 1339.5) * mm});
            skLineSegment(sketch, "E156.bottom", {"start": v(-3979, 1939.5) * mm, "end": v(-3379, 1939.5) * mm});
            skLineSegment(sketch, "E156.top", {"start": v(-3979, 1339.5) * mm, "end": v(-3379, 1339.5) * mm});
            skLineSegment(sketch, "E156.left", {"start": v(-3979, 1939.5) * mm, "end": v(-3979, 1339.5) * mm});
            skLineSegment(sketch, "E156.right", {"start": v(-3379, 1939.5) * mm, "end": v(-3379, 1339.5) * mm});
            skLineSegment(sketch, "E157.bottom", {"start": v(-3376, 1939.5) * mm, "end": v(-2776, 1939.5) * mm});
            skLineSegment(sketch, "E157.top", {"start": v(-3376, 1339.5) * mm, "end": v(-2776, 1339.5) * mm});
            skLineSegment(sketch, "E157.left", {"start": v(-3376, 1939.5) * mm, "end": v(-3376, 1339.5) * mm});
            skLineSegment(sketch, "E157.right", {"start": v(-2776, 1939.5) * mm, "end": v(-2776, 1339.5) * mm});
            skLineSegment(sketch, "E158.bottom", {"start": v(-2773, 1939.5) * mm, "end": v(-2273.75, 1939.5) * mm});
            skLineSegment(sketch, "E158.top", {"start": v(-2773, 1339.5) * mm, "end": v(-2173, 1339.5) * mm});
            skLineSegment(sketch, "E158.left", {"start": v(-2773, 1939.5) * mm, "end": v(-2773, 1339.5) * mm});
            skLineSegment(sketch, "E158.right", {"start": v(-2173, 1570) * mm, "end": v(-2173, 1339.5) * mm});
            skLineSegment(sketch, "E159.top", {"start": v(-2273.75, 1570) * mm, "end": v(-2173, 1570) * mm});
            skLineSegment(sketch, "E159.left", {"start": v(-2273.75, 1939.5) * mm, "end": v(-2273.75, 1570) * mm});
            skLineSegment(sketch, "E160.bottom", {"start": v(-4582, 1336.5) * mm, "end": v(-3982, 1336.5) * mm});
            skLineSegment(sketch, "E160.top", {"start": v(-4582, 736.5) * mm, "end": v(-3982, 736.5) * mm});
            skLineSegment(sketch, "E160.left", {"start": v(-4582, 1336.5) * mm, "end": v(-4582, 736.5) * mm});
            skLineSegment(sketch, "E160.right", {"start": v(-3979, 1336.5) * mm, "end": v(-3979, 736.5) * mm});
            skLineSegment(sketch, "E161", {"start": v(-3982, 1336.5) * mm, "end": v(-3982, 736.5) * mm});
            skLineSegment(sketch, "E162.bottom", {"start": v(-3979, 736.5) * mm, "end": v(-3379, 736.5) * mm});
            skLineSegment(sketch, "E162.top", {"start": v(-3979, 1336.5) * mm, "end": v(-3379, 1336.5) * mm});
            skLineSegment(sketch, "E162.left", {"start": v(-3979, 736.5) * mm, "end": v(-3979, 1336.5) * mm});
            skLineSegment(sketch, "E162.right", {"start": v(-3379, 736.5) * mm, "end": v(-3379, 1336.5) * mm});
            skLineSegment(sketch, "E163.bottom", {"start": v(-3376, 1336.5) * mm, "end": v(-2776, 1336.5) * mm});
            skLineSegment(sketch, "E163.top", {"start": v(-3376, 736.5) * mm, "end": v(-2776, 736.5) * mm});
            skLineSegment(sketch, "E163.left", {"start": v(-3376, 1336.5) * mm, "end": v(-3376, 736.5) * mm});
            skLineSegment(sketch, "E163.right", {"start": v(-2776, 1336.5) * mm, "end": v(-2776, 736.5) * mm});
            skLineSegment(sketch, "E164.bottom", {"start": v(-2773, 1336.5) * mm, "end": v(-2173, 1336.5) * mm});
            skLineSegment(sketch, "E164.top", {"start": v(-2773, 736.5) * mm, "end": v(-2283.88, 736.5) * mm});
            skLineSegment(sketch, "E164.left", {"start": v(-2773, 1336.5) * mm, "end": v(-2773, 736.5) * mm});
            skLineSegment(sketch, "E164.right", {"start": v(-2173, 1336.5) * mm, "end": v(-2173, 800.37) * mm});
            skLineSegment(sketch, "E165.top", {"start": v(-2283.88, 800.37) * mm, "end": v(-2173, 800.37) * mm});
            skLineSegment(sketch, "E165.left", {"start": v(-2283.88, 736.5) * mm, "end": v(-2283.88, 800.37) * mm});
            skLineSegment(sketch, "E166.bottom", {"start": v(-2170, 1339.5) * mm, "end": v(-1570, 1339.5) * mm});
            skLineSegment(sketch, "E166.top", {"start": v(-2170, 1939.5) * mm, "end": v(-1570, 1939.5) * mm});
            skLineSegment(sketch, "E166.left", {"start": v(-2170, 1339.5) * mm, "end": v(-2170, 1939.5) * mm});
            skLineSegment(sketch, "E166.right", {"start": v(-1570, 1339.5) * mm, "end": v(-1570, 1939.5) * mm});
            skLineSegment(sketch, "E167.bottom", {"start": v(-2170, 1336.5) * mm, "end": v(-1570, 1336.5) * mm});
            skLineSegment(sketch, "E167.top", {"start": v(-2170, 736.5) * mm, "end": v(-1570, 736.5) * mm});
            skLineSegment(sketch, "E167.left", {"start": v(-2170, 1336.5) * mm, "end": v(-2170, 736.5) * mm});
            skLineSegment(sketch, "E167.right", {"start": v(-1570, 1336.5) * mm, "end": v(-1570, 736.5) * mm});
            skLineSegment(sketch, "E168.bottom", {"start": v(-1567.86, 1339.5) * mm, "end": v(-967.86, 1339.5) * mm});
            skLineSegment(sketch, "E168.top", {"start": v(-1567.86, 1939.5) * mm, "end": v(-967.86, 1939.5) * mm});
            skLineSegment(sketch, "E168.left", {"start": v(-1567.86, 1339.5) * mm, "end": v(-1567.86, 1939.5) * mm});
            skLineSegment(sketch, "E168.right", {"start": v(-967.86, 1339.5) * mm, "end": v(-967.86, 1939.5) * mm});
            skLineSegment(sketch, "E169.bottom", {"start": v(-1567.86, 1336.5) * mm, "end": v(-967.86, 1336.5) * mm});
            skLineSegment(sketch, "E169.top", {"start": v(-1567.86, 736.5) * mm, "end": v(-967.86, 736.5) * mm});
            skLineSegment(sketch, "E169.left", {"start": v(-1567.86, 1336.5) * mm, "end": v(-1567.86, 736.5) * mm});
            skLineSegment(sketch, "E169.right", {"start": v(-967.86, 1336.5) * mm, "end": v(-967.86, 736.5) * mm});
            skLineSegment(sketch, "E170.bottom", {"start": v(-964.86, 1339.5) * mm, "end": v(-364.86, 1339.5) * mm});
            skLineSegment(sketch, "E170.top", {"start": v(-964.86, 1939.5) * mm, "end": v(-364.86, 1939.5) * mm});
            skLineSegment(sketch, "E170.left", {"start": v(-964.86, 1339.5) * mm, "end": v(-964.86, 1939.5) * mm});
            skLineSegment(sketch, "E170.right", {"start": v(-364.86, 1339.5) * mm, "end": v(-364.86, 1939.5) * mm});
            skLineSegment(sketch, "E171.bottom", {"start": v(-964.86, 1336.5) * mm, "end": v(-364.86, 1336.5) * mm});
            skLineSegment(sketch, "E171.top", {"start": v(-964.86, 736.5) * mm, "end": v(-364.86, 736.5) * mm});
            skLineSegment(sketch, "E171.left", {"start": v(-964.86, 1336.5) * mm, "end": v(-964.86, 736.5) * mm});
            skLineSegment(sketch, "E171.right", {"start": v(-364.86, 1336.5) * mm, "end": v(-364.86, 736.5) * mm});
            skSolve(sketch);
        }
        {
            var Q0;
            Q0=makeQuery(id+"F3.imprint","IMPRINT",FACE,{"disambiguationData":[TD([[makeQuery(id+"F3.imprint","IMPRINT",EDGE,{"derivedFrom":sQuery(id+"F3.wireOp",EDGE,"E58.bottom")}),-1.0]])]});
            var Q1;
            Q1=makeQuery(id+"F3.imprint","IMPRINT",FACE,{"disambiguationData":[TD([[makeQuery(id+"F3.imprint","IMPRINT",EDGE,{"derivedFrom":sQuery(id+"F3.wireOp",EDGE,"E60.bottom")}),-1.0]])]});
            var Q2;
            Q2=makeQuery(id+"F3.imprint","IMPRINT",FACE,{"disambiguationData":[TD([[makeQuery(id+"F3.imprint","IMPRINT",EDGE,{"derivedFrom":sQuery(id+"F3.wireOp",EDGE,"E67.bottom")}),-1.0]])]});
            var Q3;
            Q3=makeQuery(id+"F3.imprint","IMPRINT",FACE,{"disambiguationData":[TD([[makeQuery(id+"F3.imprint","IMPRINT",EDGE,{"derivedFrom":sQuery(id+"F3.wireOp",EDGE,"E68.bottom")}),-1.0]])]});
            var Q4;
            Q4=makeQuery(id+"F3.imprint","IMPRINT",FACE,{"disambiguationData":[TD([[makeQuery(id+"F3.imprint","IMPRINT",EDGE,{"derivedFrom":sQuery(id+"F3.wireOp",EDGE,"E69.bottom")}),-1.0]])]});
            var Q5;
            Q5=makeQuery(id+"F3.imprint","IMPRINT",FACE,{"disambiguationData":[TD([[makeQuery(id+"F3.imprint","IMPRINT",EDGE,{"derivedFrom":sQuery(id+"F3.wireOp",EDGE,"E77.bottom")}),1.0]])]});
            var Q6;
            Q6=makeQuery(id+"F3.imprint","IMPRINT",FACE,{"disambiguationData":[TD([[makeQuery(id+"F3.imprint","IMPRINT",EDGE,{"derivedFrom":sQuery(id+"F3.wireOp",EDGE,"E78.bottom")}),-1.0]])]});
            var Q7;
            {var subQ3=sQuery(id+"F3.wireOp",EDGE,"E65");Q7=makeQuery(id+"F3.imprint","IMPRINT",FACE,{"disambiguationData":[TD([[makeQuery(id+"F3.imprint","IMPRINT",EDGE,{"derivedFrom":subQ3}),1.0]])]});}
            var Q8;
            Q8=makeQuery(id+"F3.imprint","IMPRINT",FACE,{"disambiguationData":[TD([[makeQuery(id+"F3.imprint","IMPRINT",EDGE,{"derivedFrom":sQuery(id+"F3.wireOp",EDGE,"E62.bottom")}),1.0]])]});
            var Q9;
            {var subQ2=sQuery(id+"F3.wireOp",EDGE,"E61.top");Q9=makeQuery(id+"F3.imprint","IMPRINT",FACE,{"disambiguationData":[TD([[makeQuery(id+"F3.imprint","IMPRINT",EDGE,{"derivedFrom":subQ2}),1.0]])]});}
            extrude(context, id + "F4", {"entities" : qUnion([Q0, Q1, Q2, Q3, Q4, Q5, Q6, Q7, Q8, Q9]), "depth" : 6 * mm, "offsetDistance" : 25 * mm});
        }
        {
            var Q0;
            {var subQ1=sQuery(id+"F3.wireOp",EDGE,"E70.bottom");Q0=makeQuery(id+"F3.imprint","IMPRINT",FACE,{"disambiguationData":[TD([[makeQuery(id+"F3.imprint","IMPRINT",EDGE,{"derivedFrom":subQ1}),-1.0]])]});}
            var Q1;
            Q1=makeQuery(id+"F3.imprint","IMPRINT",FACE,{"disambiguationData":[TD([[makeQuery(id+"F3.imprint","IMPRINT",EDGE,{"derivedFrom":sQuery(id+"F3.wireOp",EDGE,"E79.bottom")}),1.0]])]});
            extrude(context, id + "F5", {"entities" : qUnion([Q0, Q1]), "depth" : 6 * mm, "offsetDistance" : 25 * mm});
        }
    });
